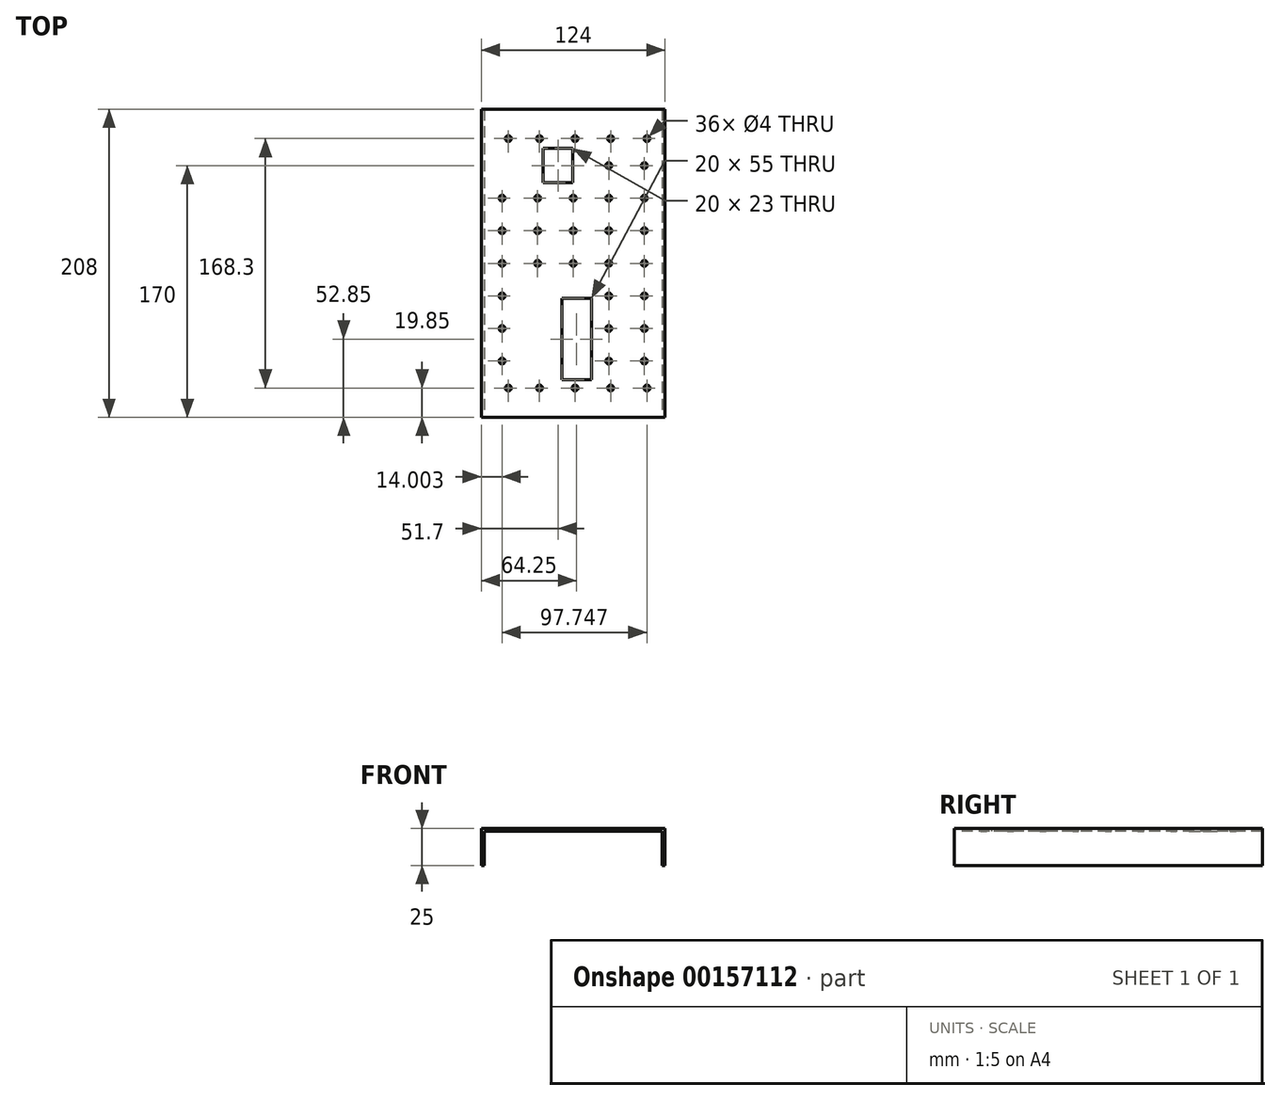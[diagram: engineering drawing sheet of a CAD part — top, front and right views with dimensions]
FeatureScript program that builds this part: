
annotation { "Feature Type Name" : "Feature", "Feature Type Description" : "" }
export const myFeature = defineFeature(function(context is Context, id is Id, definition is map)
    precondition{}
    {
        {
            var Q0;
            Q0=qCreatedBy(makeId("Top.planeOp"),FACE);
            var sketch = newSketch(context, id + "F0", { "sketchPlane" : qUnion([Q0])});
            skLineSegment(sketch, "E0.bottom", {"start": v(57, 110) * mm, "end": v(-57, 110) * mm, "construction": true});
            skLineSegment(sketch, "E0.top", {"start": v(57, -110) * mm, "end": v(-57, -110) * mm, "construction": true});
            skLineSegment(sketch, "E0.left", {"start": v(57, 110) * mm, "end": v(57, -110) * mm, "construction": true});
            skLineSegment(sketch, "E0.right", {"start": v(-57, 110) * mm, "end": v(-57, -110) * mm, "construction": true});
            skPoint(sketch, "E0.middle", {"position": v(0, 0) * mm});
            skLineSegment(sketch, "E1.bottom", {"start": v(47.25, 84.15) * mm, "end": v(-47.25, 84.15) * mm, "construction": true});
            skLineSegment(sketch, "E1.top", {"start": v(47.25, -84.15) * mm, "end": v(-47.25, -84.15) * mm, "construction": true});
            skLineSegment(sketch, "E1.left", {"start": v(47.25, 84.15) * mm, "end": v(47.25, -84.15) * mm, "construction": true});
            skLineSegment(sketch, "E1.right", {"start": v(-47.25, 84.15) * mm, "end": v(-47.25, -84.15) * mm, "construction": true});
            skLineSegment(sketch, "E2.0", {"start": v(62, 115) * mm, "end": v(62, -115) * mm});
            skLineSegment(sketch, "E2.1", {"start": v(62, 115) * mm, "end": v(-62, 115) * mm});
            skLineSegment(sketch, "E2.2", {"start": v(-62, 115) * mm, "end": v(-62, -115) * mm});
            skLineSegment(sketch, "E2.3", {"start": v(62, -115) * mm, "end": v(-62, -115) * mm});
            skLineSegment(sketch, "E3.0", {"start": v(60, 113) * mm, "end": v(60, -113) * mm});
            skLineSegment(sketch, "E3.1", {"start": v(60, 113) * mm, "end": v(-60, 113) * mm});
            skLineSegment(sketch, "E3.2", {"start": v(-60, 113) * mm, "end": v(-60, -113) * mm});
            skLineSegment(sketch, "E3.3", {"start": v(60, -113) * mm, "end": v(-60, -113) * mm});
            skLineSegment(sketch, "E4", {"start": v(-47.25, -84.15) * mm, "end": v(-46.75, -84.15) * mm});
            skLineSegment(sketch, "E5", {"start": v(46.75, -84.15) * mm, "end": v(47.25, -84.15) * mm});
            skLineSegment(sketch, "E6", {"start": v(47.25, 84.15) * mm, "end": v(46.75, 84.15) * mm});
            skLineSegment(sketch, "E7", {"start": v(-47.25, 84.15) * mm, "end": v(-46.75, 84.15) * mm});
            skLineSegment(sketch, "E8.direction1", {"start": v(46.75, -84.15) * mm, "end": v(14.75, -84.15) * mm, "construction": true});
            skLineSegment(sketch, "E9.direction1", {"start": v(46.75, 84.15) * mm, "end": v(21.75, 84.15) * mm, "construction": true});
            skCircle(sketch, "E10", {"center": v(0, -0.01) * mm, "radius": 2 * mm});
            skCircle(sketch, "E11.0.1.0", {"center": v(0, 21.99) * mm, "radius": 2 * mm});
            skCircle(sketch, "E11.0.2.0", {"center": v(0, 43.99) * mm, "radius": 2 * mm});
            skCircle(sketch, "E11.1.0.0", {"center": v(24, -0.01) * mm, "radius": 2 * mm});
            skCircle(sketch, "E11.1.1.0", {"center": v(24, 21.99) * mm, "radius": 2 * mm});
            skCircle(sketch, "E11.1.2.0", {"center": v(24, 43.99) * mm, "radius": 2 * mm});
            skCircle(sketch, "E11.1.3.0", {"center": v(24, 65.99) * mm, "radius": 2 * mm});
            skCircle(sketch, "E11.2.0.0", {"center": v(48, -0.01) * mm, "radius": 2 * mm});
            skCircle(sketch, "E11.2.1.0", {"center": v(48, 21.99) * mm, "radius": 2 * mm});
            skCircle(sketch, "E11.2.2.0", {"center": v(48, 43.99) * mm, "radius": 2 * mm});
            skCircle(sketch, "E11.2.3.0", {"center": v(48, 65.99) * mm, "radius": 2 * mm});
            skLineSegment(sketch, "E11.direction1", {"start": v(0, -0.01) * mm, "end": v(24, -0.01) * mm, "construction": true});
            skLineSegment(sketch, "E11.direction2", {"start": v(0, -0.01) * mm, "end": v(0, 21.99) * mm, "construction": true});
            skCircle(sketch, "E12.1.0.0", {"center": v(-24, -0.01) * mm, "radius": 2 * mm});
            skCircle(sketch, "E12.2.0.0", {"center": v(-48, -0.01) * mm, "radius": 2 * mm});
            skLineSegment(sketch, "E12.direction1", {"start": v(0, -0.01) * mm, "end": v(-24, -0.01) * mm, "construction": true});
            skCircle(sketch, "E13.1.0.0", {"center": v(-24, 21.99) * mm, "radius": 2 * mm});
            skCircle(sketch, "E13.2.0.0", {"center": v(-48, 21.99) * mm, "radius": 2 * mm});
            skLineSegment(sketch, "E13.direction1", {"start": v(0, 21.99) * mm, "end": v(-24, 21.99) * mm, "construction": true});
            skCircle(sketch, "E14.0.1.0", {"center": v(-48, -22.01) * mm, "radius": 2 * mm});
            skCircle(sketch, "E14.0.2.0", {"center": v(-48, -44.01) * mm, "radius": 2 * mm});
            skCircle(sketch, "E14.0.3.0", {"center": v(-48, -66.01) * mm, "radius": 2 * mm});
            skLineSegment(sketch, "E14.direction1", {"start": v(-48, -0.01) * mm, "end": v(-73, -0.01) * mm, "construction": true});
            skLineSegment(sketch, "E14.direction2", {"start": v(-48, -0.01) * mm, "end": v(-48, -22.01) * mm, "construction": true});
            skCircle(sketch, "E15.0.1.0", {"center": v(24, -22.01) * mm, "radius": 2 * mm});
            skCircle(sketch, "E15.0.2.0", {"center": v(24, -44.01) * mm, "radius": 2 * mm});
            skCircle(sketch, "E15.0.3.0", {"center": v(24, -66.01) * mm, "radius": 2 * mm});
            skCircle(sketch, "E15.1.1.0", {"center": v(48, -22.01) * mm, "radius": 2 * mm});
            skCircle(sketch, "E15.1.2.0", {"center": v(48, -44.01) * mm, "radius": 2 * mm});
            skCircle(sketch, "E15.1.3.0", {"center": v(48, -66.01) * mm, "radius": 2 * mm});
            skLineSegment(sketch, "E15.direction1", {"start": v(24, -0.01) * mm, "end": v(48, -0.01) * mm, "construction": true});
            skLineSegment(sketch, "E15.direction2", {"start": v(24, -0.01) * mm, "end": v(24, -22.01) * mm, "construction": true});
            skCircle(sketch, "E16.1.0.0", {"center": v(-24, 43.99) * mm, "radius": 2 * mm});
            skCircle(sketch, "E16.2.0.0", {"center": v(-48, 43.99) * mm, "radius": 2 * mm});
            skLineSegment(sketch, "E16.direction1", {"start": v(0, 43.99) * mm, "end": v(-24, 43.99) * mm, "construction": true});
            skCircle(sketch, "E17.1.0.0", {"center": v(-22.75, -84.15) * mm, "radius": 2 * mm});
            skCircle(sketch, "E17.2.0.0", {"center": v(1.25, -84.15) * mm, "radius": 2 * mm});
            skCircle(sketch, "E17.3.0.0", {"center": v(25.25, -84.15) * mm, "radius": 2 * mm});
            skLineSegment(sketch, "E17.direction1", {"start": v(-46.75, -84.15) * mm, "end": v(-22.75, -84.15) * mm, "construction": true});
            skCircle(sketch, "E18.1.0.0", {"center": v(-22.75, 84.15) * mm, "radius": 2 * mm});
            skCircle(sketch, "E18.2.0.0", {"center": v(1.25, 84.15) * mm, "radius": 2 * mm});
            skCircle(sketch, "E18.3.0.0", {"center": v(25.25, 84.15) * mm, "radius": 2 * mm});
            skLineSegment(sketch, "E18.direction1", {"start": v(-46.75, 84.15) * mm, "end": v(-22.75, 84.15) * mm, "construction": true});
            skCircle(sketch, "E19", {"center": v(-43.75, -84.15) * mm, "radius": 2 * mm});
            skCircle(sketch, "E20", {"center": v(49.75, -84.15) * mm, "radius": 2 * mm});
            skCircle(sketch, "E21", {"center": v(-43.75, 84.15) * mm, "radius": 2 * mm});
            skCircle(sketch, "E22", {"center": v(49.75, 84.15) * mm, "radius": 2 * mm});
            skLineSegment(sketch, "E23.0", {"start": v(-7.75, -23.65) * mm, "end": v(-7.75, -78.65) * mm});
            skLineSegment(sketch, "E23.1", {"start": v(-7.75, -23.65) * mm, "end": v(12.25, -23.65) * mm});
            skLineSegment(sketch, "E23.2", {"start": v(12.25, -23.65) * mm, "end": v(12.25, -78.65) * mm});
            skLineSegment(sketch, "E23.3", {"start": v(-7.75, -78.65) * mm, "end": v(12.25, -78.65) * mm});
            skLineSegment(sketch, "E24.0", {"start": v(-0.3, 77.5) * mm, "end": v(-20.3, 77.5) * mm});
            skLineSegment(sketch, "E24.1", {"start": v(-0.3, 54.5) * mm, "end": v(-0.3, 77.5) * mm});
            skLineSegment(sketch, "E24.2", {"start": v(-0.3, 54.5) * mm, "end": v(-20.3, 54.5) * mm});
            skLineSegment(sketch, "E24.3", {"start": v(-20.3, 54.5) * mm, "end": v(-20.3, 77.5) * mm});
            skSolve(sketch);
        }
        {
            var Q0;
            Q0=makeQuery(id+"F0.imprint","IMPRINT",FACE,{"disambiguationData":[TD([[makeQuery(id+"F0.imprint","IMPRINT",EDGE,{"derivedFrom":sQuery(id+"F0.wireOp",EDGE,"E2.0")}),-1.0]])]});
            extrude(context, id + "F1", {"entities" : qUnion([Q0]), "oppositeDirection" : true, "depth" : 25 * mm});
        }
        {
            var Q0;
            Q0=makeQuery(id+"F0.imprint","IMPRINT",FACE,{"disambiguationData":[TD([[makeQuery(id+"F0.imprint","IMPRINT",EDGE,{"derivedFrom":sQuery(id+"F0.wireOp",EDGE,"E3.0")}),-1.0]])]});
            extrude(context, id + "F2", {"entities" : qUnion([Q0]), "operationType" : NewBodyOperationType.ADD, "oppositeDirection" : true, "depth" : 2 * mm});
        }
        {
            var Q0;
            Q0=makeQuery(id+"F1.opExtrude","SWEPT_FACE",FACE,{"disambiguationData":[OSD([sQuery(id+"F0.wireOp",EDGE,"E2.2")])]});
            var sketch = newSketch(context, id + "F3", { "sketchPlane" : qUnion([Q0])});
            skCircle(sketch, "E25", {"center": v(0, -12.5) * mm, "radius": 4 * mm});
            skCircle(sketch, "E26.1.0.0", {"center": v(27, -12.5) * mm, "radius": 4 * mm});
            skCircle(sketch, "E26.2.0.0", {"center": v(54, -12.5) * mm, "radius": 4 * mm});
            skCircle(sketch, "E26.3.0.0", {"center": v(81, -12.5) * mm, "radius": 4 * mm});
            skLineSegment(sketch, "E26.direction1", {"start": v(0, -12.5) * mm, "end": v(27, -12.5) * mm, "construction": true});
            skCircle(sketch, "E27.1.0.0", {"center": v(-27, -12.5) * mm, "radius": 4 * mm});
            skCircle(sketch, "E27.2.0.0", {"center": v(-54, -12.5) * mm, "radius": 4 * mm});
            skCircle(sketch, "E27.3.0.0", {"center": v(-81, -12.5) * mm, "radius": 4 * mm});
            skLineSegment(sketch, "E27.direction1", {"start": v(0, -12.5) * mm, "end": v(-27, -12.5) * mm, "construction": true});
            skSolve(sketch);
        }
        {
            var Q0;
            Q0=makeQuery(id+"F1.opExtrude","SWEPT_FACE",FACE,{"disambiguationData":[OSD([sQuery(id+"F0.wireOp",EDGE,"E2.0")])]});
            var sketch = newSketch(context, id + "F4", { "sketchPlane" : qUnion([Q0])});
            skLineSegment(sketch, "E28.bottom", {"start": v(115, 20.74) * mm, "end": v(104, 20.74) * mm});
            skLineSegment(sketch, "E28.top", {"start": v(115, -88.09) * mm, "end": v(104, -88.09) * mm});
            skLineSegment(sketch, "E28.left", {"start": v(115, 20.74) * mm, "end": v(115, -88.09) * mm});
            skLineSegment(sketch, "E28.right", {"start": v(104, 20.74) * mm, "end": v(104, -88.09) * mm});
            skLineSegment(sketch, "E29.bottom", {"start": v(104, -53) * mm, "end": v(-115, -53) * mm});
            skLineSegment(sketch, "E29.top", {"start": v(104, -88.09) * mm, "end": v(-115, -88.09) * mm});
            skLineSegment(sketch, "E29.left", {"start": v(104, -53) * mm, "end": v(104, -88.09) * mm});
            skLineSegment(sketch, "E29.right", {"start": v(-115, -53) * mm, "end": v(-115, -88.09) * mm});
            skLineSegment(sketch, "E30.bottom", {"start": v(-104, -53) * mm, "end": v(-115, -53) * mm});
            skLineSegment(sketch, "E30.top", {"start": v(-104, 21.71) * mm, "end": v(-115, 21.71) * mm});
            skLineSegment(sketch, "E30.left", {"start": v(-104, -53) * mm, "end": v(-104, 21.71) * mm});
            skLineSegment(sketch, "E30.right", {"start": v(-115, -53) * mm, "end": v(-115, 21.71) * mm});
            skSolve(sketch);
        }
        {
            var Q0;
            Q0 = qSketchRegion(id + "F4", true);
            extrude(context, id + "F5", {"entities" : qUnion([Q0]), "operationType" : NewBodyOperationType.REMOVE, "oppositeDirection" : true, "depth" : 150 * mm});
        }
    });
